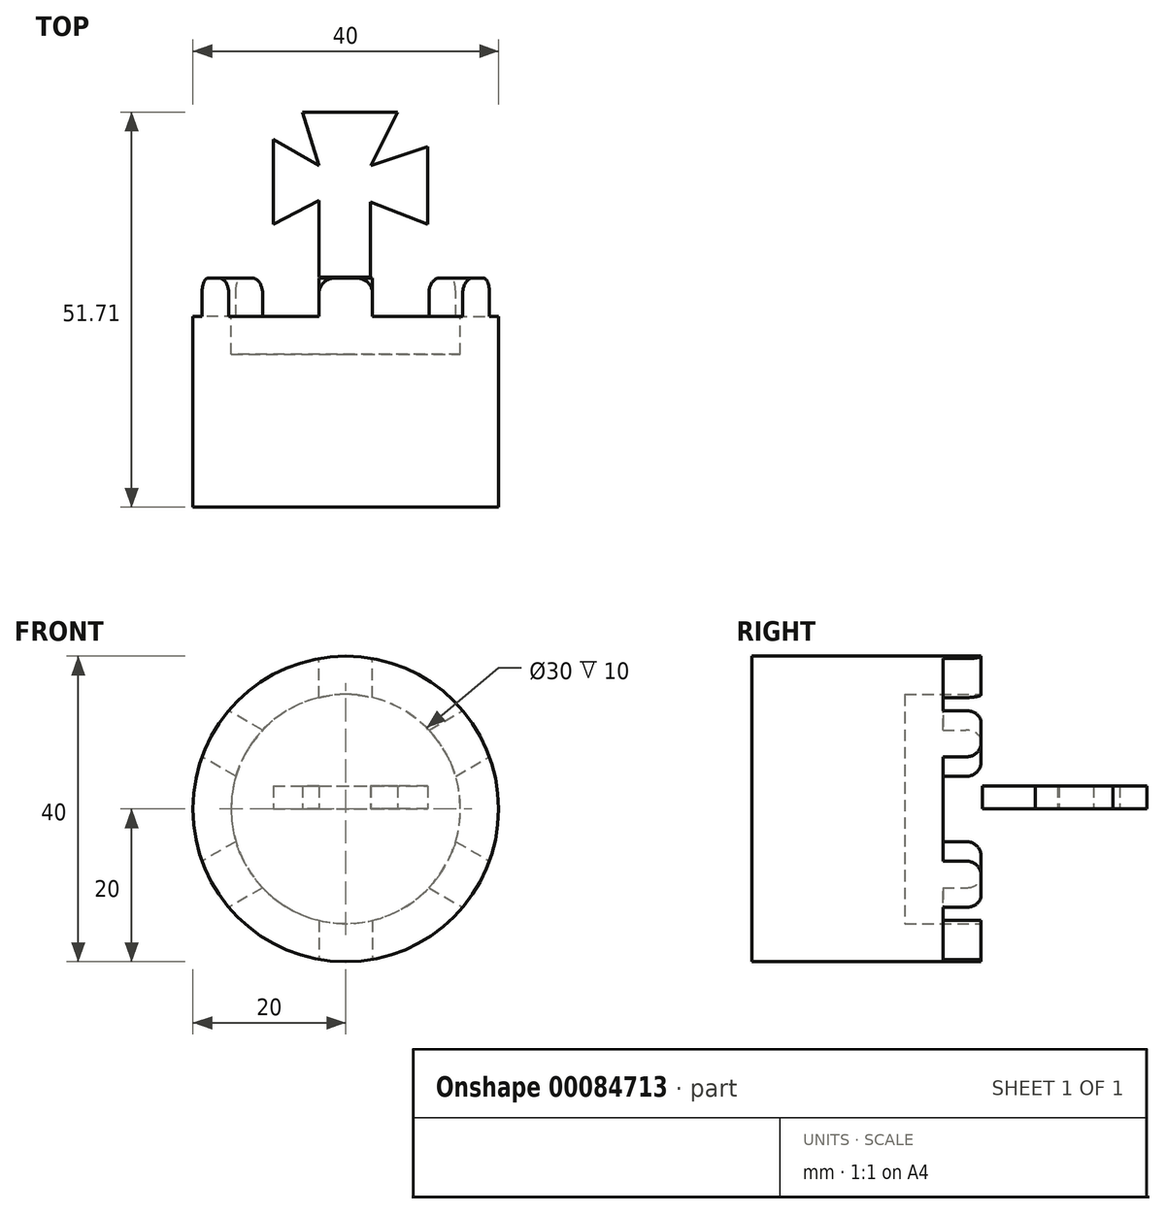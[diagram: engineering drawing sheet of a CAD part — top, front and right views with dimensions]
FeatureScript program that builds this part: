
annotation { "Feature Type Name" : "Feature", "Feature Type Description" : "" }
export const myFeature = defineFeature(function(context is Context, id is Id, definition is map)
    precondition{}
    {
        {
            var Q0;
            Q0=qCreatedBy(makeId("Front.planeOp"),FACE);
            var sketch = newSketch(context, id + "F0", { "sketchPlane" : qUnion([Q0])});
            skCircle(sketch, "E0", {"center": v(0, 0) * mm, "radius": 20 * mm});
            skSolve(sketch);
        }
        {
            var Q0;
            Q0=makeQuery(id+"F0.imprint","IMPRINT",FACE,{"disambiguationData":[TD([[makeQuery(id+"F0.imprint","IMPRINT",EDGE,{"derivedFrom":sQuery(id+"F0.wireOp",EDGE,"E0")}),1.0]])]});
            extrude(context, id + "F1", {"entities" : qUnion([Q0]), "oppositeDirection" : true, "depth" : 30 * mm});
        }
        {
            var Q0;
            Q0=makeQuery(id+"F1.opExtrude","CAP_FACE",FACE,{"disambiguationData":[OSD([sQuery(id+"F0.wireOp",EDGE,"E0")])],"isStart":false});
            var sketch = newSketch(context, id + "F2", { "sketchPlane" : qUnion([Q0])});
            skCircle(sketch, "E1", {"center": v(0, 0) * mm, "radius": 15 * mm});
            skSolve(sketch);
        }
        {
            var Q0;
            Q0=qSketchRegion(id+"F2",true);
            extrude(context, id + "F3", {"entities" : qUnion([Q0]), "operationType" : NewBodyOperationType.REMOVE, "oppositeDirection" : true, "depth" : 10 * mm});
        }
        {
            var Q0;
            Q0=makeQuery(id+"F1.opExtrude","CAP_FACE",FACE,{"disambiguationData":[OSD([sQuery(id+"F0.wireOp",EDGE,"E0")])],"isStart":false});
            var sketch = newSketch(context, id + "F4", { "sketchPlane" : qUnion([Q0])});
            skLineSegment(sketch, "E2.bottom", {"start": v(-3.5, -14.59) * mm, "end": v(3.5, -14.59) * mm});
            skLineSegment(sketch, "E2.top", {"start": v(-3.5, -19.7) * mm, "end": v(3.5, -19.7) * mm, "construction": true});
            skLineSegment(sketch, "E2.left", {"start": v(-3.5, -14.59) * mm, "end": v(-3.5, -19.7) * mm});
            skLineSegment(sketch, "E2.right", {"start": v(3.5, -14.59) * mm, "end": v(3.5, -19.7) * mm});
            skLineSegment(sketch, "E3", {"start": v(0, -19.7) * mm, "end": v(0, 0) * mm, "construction": true});
            skArc(sketch, "E4", {"start": v(-3.5, -19.7) * mm, "mid": v(0, -20) * mm, "end": v(3.5, -19.7) * mm});
            skLineSegment(sketch, "E5.1.0", {"start": v(10.88, -10.32) * mm, "end": v(15.3, -12.88) * mm});
            skLineSegment(sketch, "E5.1.1", {"start": v(10.88, -10.32) * mm, "end": v(14.38, -4.26) * mm});
            skLineSegment(sketch, "E5.1.2", {"start": v(15.3, -12.88) * mm, "end": v(18.8, -6.81) * mm, "construction": true});
            skLineSegment(sketch, "E5.1.3", {"start": v(14.38, -4.26) * mm, "end": v(18.8, -6.81) * mm});
            skArc(sketch, "E5.1.4", {"start": v(15.3, -12.88) * mm, "mid": v(17.32, -10) * mm, "end": v(18.8, -6.81) * mm});
            skLineSegment(sketch, "E5.2.0", {"start": v(14.38, 4.26) * mm, "end": v(18.8, 6.81) * mm});
            skLineSegment(sketch, "E5.2.1", {"start": v(14.38, 4.26) * mm, "end": v(10.88, 10.32) * mm});
            skLineSegment(sketch, "E5.2.2", {"start": v(18.8, 6.81) * mm, "end": v(15.3, 12.88) * mm, "construction": true});
            skLineSegment(sketch, "E5.2.3", {"start": v(10.88, 10.32) * mm, "end": v(15.3, 12.88) * mm});
            skArc(sketch, "E5.2.4", {"start": v(18.8, 6.81) * mm, "mid": v(17.32, 10) * mm, "end": v(15.3, 12.88) * mm});
            skLineSegment(sketch, "E5.3.0", {"start": v(3.5, 14.59) * mm, "end": v(3.5, 19.7) * mm});
            skLineSegment(sketch, "E5.3.1", {"start": v(3.5, 14.59) * mm, "end": v(-3.5, 14.59) * mm});
            skLineSegment(sketch, "E5.3.2", {"start": v(3.5, 19.7) * mm, "end": v(-3.5, 19.7) * mm, "construction": true});
            skLineSegment(sketch, "E5.3.3", {"start": v(-3.5, 14.59) * mm, "end": v(-3.5, 19.7) * mm});
            skArc(sketch, "E5.3.4", {"start": v(3.5, 19.7) * mm, "mid": v(0, 20) * mm, "end": v(-3.5, 19.7) * mm});
            skLineSegment(sketch, "E5.4.0", {"start": v(-10.88, 10.32) * mm, "end": v(-15.3, 12.88) * mm});
            skLineSegment(sketch, "E5.4.1", {"start": v(-10.88, 10.32) * mm, "end": v(-14.38, 4.26) * mm});
            skLineSegment(sketch, "E5.4.2", {"start": v(-15.3, 12.88) * mm, "end": v(-18.8, 6.81) * mm, "construction": true});
            skLineSegment(sketch, "E5.4.3", {"start": v(-14.38, 4.26) * mm, "end": v(-18.8, 6.81) * mm});
            skArc(sketch, "E5.4.4", {"start": v(-15.3, 12.88) * mm, "mid": v(-17.32, 10) * mm, "end": v(-18.8, 6.81) * mm});
            skLineSegment(sketch, "E5.5.0", {"start": v(-14.38, -4.26) * mm, "end": v(-18.8, -6.81) * mm});
            skLineSegment(sketch, "E5.5.1", {"start": v(-14.38, -4.26) * mm, "end": v(-10.88, -10.32) * mm});
            skLineSegment(sketch, "E5.5.2", {"start": v(-18.8, -6.81) * mm, "end": v(-15.3, -12.88) * mm, "construction": true});
            skLineSegment(sketch, "E5.5.3", {"start": v(-10.88, -10.32) * mm, "end": v(-15.3, -12.88) * mm});
            skArc(sketch, "E5.5.4", {"start": v(-18.8, -6.81) * mm, "mid": v(-17.32, -10) * mm, "end": v(-15.3, -12.88) * mm});
            skSolve(sketch);
        }
        {
            var Q0;
            {var subQ0=sQuery(id+"F4.wireOp",EDGE,"E2.left");var subQ3=makeQuery(id+"F1.opExtrude","CAP_EDGE",EDGE,{"disambiguationData":[OSD([sQuery(id+"F0.wireOp",EDGE,"E0")])],"isStart":false});var subQ4=makeQuery(id+"F4.imprint","INTERSECT",VERTEX,{"derivedFrom":[subQ3,subQ0]});Q0=makeQuery(id+"F4.imprint","IMPRINT",FACE,{"disambiguationData":[TD([[makeQuery(id+"F4.imprint","IMPRINT",EDGE,{"disambiguationData":[TD([[subQ4,1.0]])],"derivedFrom":subQ0}),-1.0]])]});}
            var Q1;
            {var subQ0=sQuery(id+"F4.wireOp",EDGE,"E5.4.3");Q1=makeQuery(id+"F4.imprint","IMPRINT",FACE,{"disambiguationData":[TD([[makeQuery(id+"F4.imprint","IMPRINT",EDGE,{"derivedFrom":subQ0}),1.0]])]});}
            var Q2;
            {var subQ0=sQuery(id+"F4.wireOp",EDGE,"E5.3.3");Q2=makeQuery(id+"F4.imprint","IMPRINT",FACE,{"disambiguationData":[TD([[makeQuery(id+"F4.imprint","IMPRINT",EDGE,{"derivedFrom":subQ0}),1.0]])]});}
            var Q3;
            {var subQ0=sQuery(id+"F4.wireOp",EDGE,"E5.2.3");Q3=makeQuery(id+"F4.imprint","IMPRINT",FACE,{"disambiguationData":[TD([[makeQuery(id+"F4.imprint","IMPRINT",EDGE,{"derivedFrom":subQ0}),1.0]])]});}
            var Q4;
            {var subQ0=sQuery(id+"F4.wireOp",EDGE,"E5.1.3");Q4=makeQuery(id+"F4.imprint","IMPRINT",FACE,{"disambiguationData":[TD([[makeQuery(id+"F4.imprint","IMPRINT",EDGE,{"derivedFrom":subQ0}),1.0]])]});}
            var Q5;
            {var subQ0=sQuery(id+"F4.wireOp",EDGE,"E2.right");Q5=makeQuery(id+"F4.imprint","IMPRINT",FACE,{"disambiguationData":[TD([[makeQuery(id+"F4.imprint","IMPRINT",EDGE,{"derivedFrom":subQ0}),1.0]])]});}
            extrude(context, id + "F5", {"entities" : qUnion([Q0, Q1, Q2, Q3, Q4, Q5]), "operationType" : NewBodyOperationType.REMOVE, "oppositeDirection" : true, "depth" : 5 * mm});
        }
        {
            var Q0;
            Q0=makeQuery(id+"F5.boolean.opBoolean","COPY",EDGE,{"derivedFrom":makeQuery(id+"F5.opExtrude","CAP_EDGE",EDGE,{"disambiguationData":[OSD([sQuery(id+"F4.wireOp",EDGE,"E2.right")])],"isStart":true})});
            var Q1;
            Q1=makeQuery(id+"F5.boolean.opBoolean","COPY",EDGE,{"derivedFrom":makeQuery(id+"F5.opExtrude","CAP_EDGE",EDGE,{"disambiguationData":[OSD([sQuery(id+"F4.wireOp",EDGE,"E2.left")])],"isStart":true})});
            var Q2;
            Q2=makeQuery(id+"F5.boolean.opBoolean","COPY",EDGE,{"derivedFrom":makeQuery(id+"F5.opExtrude","CAP_EDGE",EDGE,{"disambiguationData":[OSD([sQuery(id+"F4.wireOp",EDGE,"E5.5.3")])],"isStart":true})});
            var Q3;
            Q3=makeQuery(id+"F5.boolean.opBoolean","COPY",EDGE,{"derivedFrom":makeQuery(id+"F5.opExtrude","CAP_EDGE",EDGE,{"disambiguationData":[OSD([sQuery(id+"F4.wireOp",EDGE,"E5.5.0")])],"isStart":true})});
            var Q4;
            Q4=makeQuery(id+"F5.boolean.opBoolean","COPY",EDGE,{"derivedFrom":makeQuery(id+"F5.opExtrude","CAP_EDGE",EDGE,{"disambiguationData":[OSD([sQuery(id+"F4.wireOp",EDGE,"E5.4.3")])],"isStart":true})});
            var Q5;
            Q5=makeQuery(id+"F5.boolean.opBoolean","COPY",EDGE,{"derivedFrom":makeQuery(id+"F5.opExtrude","CAP_EDGE",EDGE,{"disambiguationData":[OSD([sQuery(id+"F4.wireOp",EDGE,"E5.3.3")])],"isStart":true})});
            var Q6;
            Q6=makeQuery(id+"F5.boolean.opBoolean","COPY",EDGE,{"derivedFrom":makeQuery(id+"F5.opExtrude","CAP_EDGE",EDGE,{"disambiguationData":[OSD([sQuery(id+"F4.wireOp",EDGE,"E5.3.0")])],"isStart":true})});
            var Q7;
            Q7=makeQuery(id+"F5.boolean.opBoolean","COPY",EDGE,{"derivedFrom":makeQuery(id+"F5.opExtrude","CAP_EDGE",EDGE,{"disambiguationData":[OSD([sQuery(id+"F4.wireOp",EDGE,"E5.2.3")])],"isStart":true})});
            var Q8;
            Q8=makeQuery(id+"F5.boolean.opBoolean","COPY",EDGE,{"derivedFrom":makeQuery(id+"F5.opExtrude","CAP_EDGE",EDGE,{"disambiguationData":[OSD([sQuery(id+"F4.wireOp",EDGE,"E5.2.0")])],"isStart":true})});
            var Q9;
            Q9=makeQuery(id+"F5.boolean.opBoolean","COPY",EDGE,{"derivedFrom":makeQuery(id+"F5.opExtrude","CAP_EDGE",EDGE,{"disambiguationData":[OSD([sQuery(id+"F4.wireOp",EDGE,"E5.1.3")])],"isStart":true})});
            var Q10;
            Q10=makeQuery(id+"F5.boolean.opBoolean","COPY",EDGE,{"derivedFrom":makeQuery(id+"F5.opExtrude","CAP_EDGE",EDGE,{"disambiguationData":[OSD([sQuery(id+"F4.wireOp",EDGE,"E5.1.0")])],"isStart":true})});
            var Q11;
            Q11=makeQuery(id+"F5.boolean.opBoolean","COPY",EDGE,{"derivedFrom":makeQuery(id+"F5.opExtrude","CAP_EDGE",EDGE,{"disambiguationData":[OSD([sQuery(id+"F4.wireOp",EDGE,"E5.4.0")])],"isStart":true})});
            fillet(context, id + "F6", {"entities" : qUnion([Q0, Q1, Q2, Q3, Q4, Q5, Q6, Q7, Q8, Q9, Q10, Q11]), "radius" : 2 * mm, "tangentPropagation" : true, "allowEdgeOverflow" : false});
        }
        {
            var Q0;
            Q0=qCreatedBy(makeId("Top.planeOp"),FACE);
            var sketch = newSketch(context, id + "F7", { "sketchPlane" : qUnion([Q0])});
            skLineSegment(sketch, "E6", {"start": v(-3.51, 30.13) * mm, "end": v(-3.51, 40.17) * mm});
            skLineSegment(sketch, "E7", {"start": v(-3.51, 40.17) * mm, "end": v(-9.47, 37.06) * mm});
            skLineSegment(sketch, "E8", {"start": v(-9.47, 37.06) * mm, "end": v(-9.47, 48.14) * mm});
            skLineSegment(sketch, "E9", {"start": v(-9.47, 48.14) * mm, "end": v(-3.51, 44.7) * mm});
            skLineSegment(sketch, "E10", {"start": v(-3.51, 44.7) * mm, "end": v(-5.65, 51.7) * mm});
            skLineSegment(sketch, "E11", {"start": v(-5.65, 51.7) * mm, "end": v(6.8, 51.7) * mm});
            skLineSegment(sketch, "E12", {"start": v(6.8, 51.7) * mm, "end": v(3.3, 44.7) * mm});
            skLineSegment(sketch, "E13", {"start": v(3.3, 44.7) * mm, "end": v(10.74, 47.24) * mm});
            skLineSegment(sketch, "E14", {"start": v(10.74, 47.24) * mm, "end": v(10.74, 37.06) * mm});
            skLineSegment(sketch, "E15", {"start": v(10.74, 37.06) * mm, "end": v(3.23, 39.98) * mm});
            skLineSegment(sketch, "E16", {"start": v(3.23, 39.98) * mm, "end": v(3.23, 30.2) * mm});
            skLineSegment(sketch, "E17", {"start": v(-3.51, 30.13) * mm, "end": v(3.23, 30.2) * mm});
            skSolve(sketch);
        }
        {
            var Q0;
            Q0=qSketchRegion(id+"F7",true);
            extrude(context, id + "F8", {"entities" : qUnion([Q0]), "depth" : 3 * mm});
        }
    });
